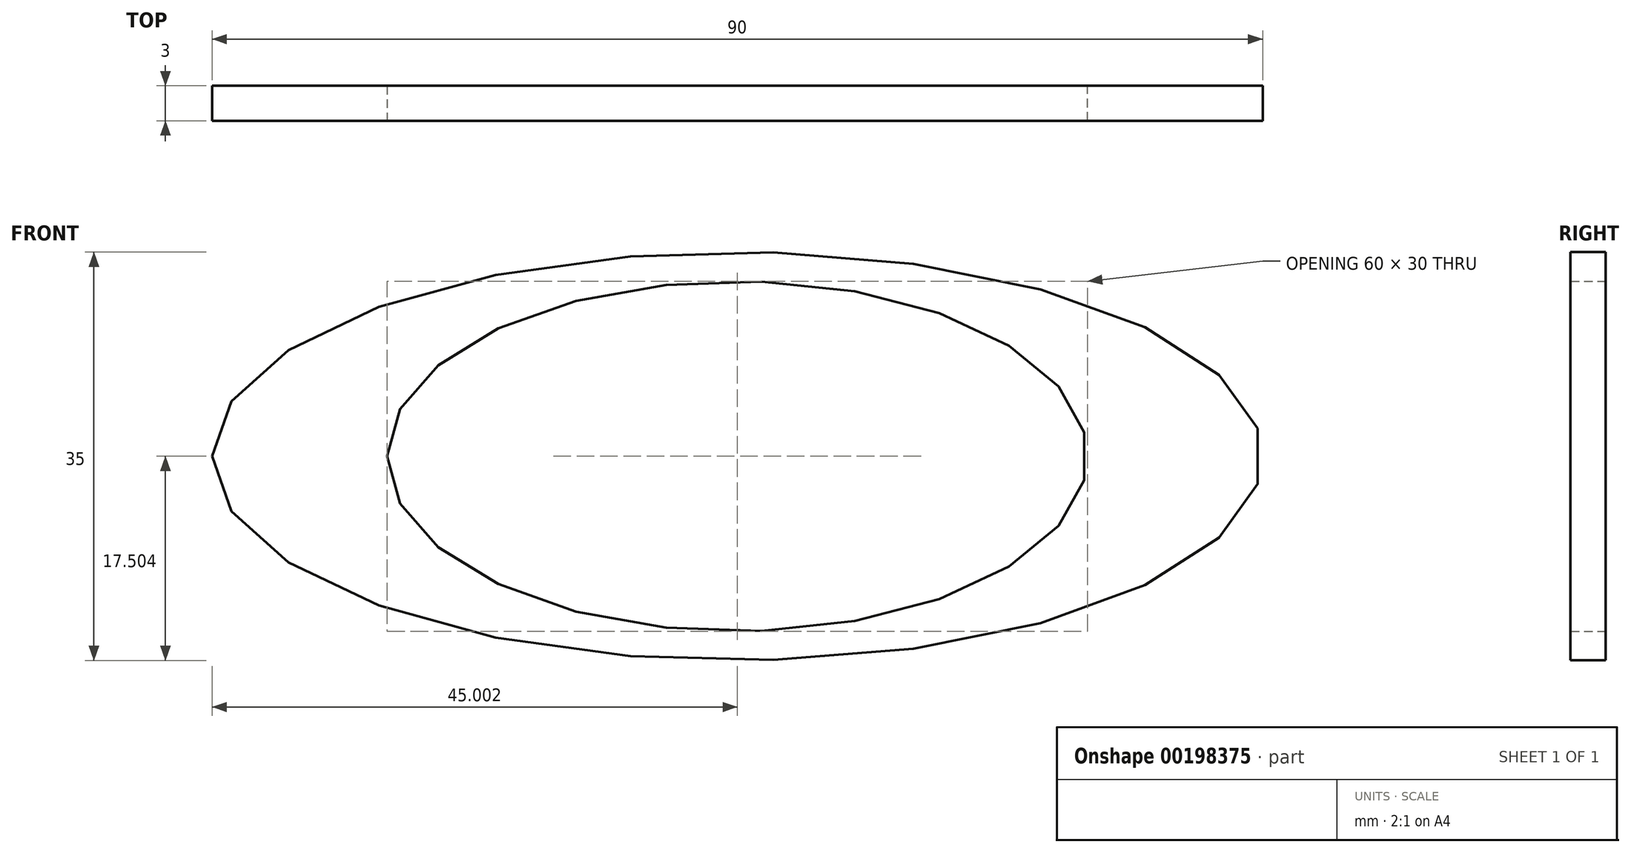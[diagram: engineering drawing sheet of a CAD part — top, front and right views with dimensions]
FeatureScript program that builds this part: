
annotation { "Feature Type Name" : "Feature", "Feature Type Description" : "" }
export const myFeature = defineFeature(function(context is Context, id is Id, definition is map)
    precondition{}
    {
        {
            var Q0;
            Q0=qCreatedBy(makeId("Front.planeOp"),FACE);
            var sketch = newSketch(context, id + "F0", { "sketchPlane" : qUnion([Q0])});
            skEllipse(sketch, "E0", {"center": v(-9.7, -46.2) * mm, "majorRadius": 45 * mm, "minorRadius": 17.5 * mm, "majorAxis": v(-1, 0)});
            skSolve(sketch);
        }
        {
            var Q0;
            Q0=qSketchRegion(id+"F0",true);
            extrude(context, id + "F1", {"entities" : qUnion([Q0]), "depth" : 3 * mm});
        }
        {
            var Q0;
            Q0=makeQuery(id+"F1.opExtrude","CAP_FACE",FACE,{"disambiguationData":[OSD([sQuery(id+"F0.wireOp",EDGE,"E0")])],"isStart":false});
            var sketch = newSketch(context, id + "F2", { "sketchPlane" : qUnion([Q0])});
            skEllipse(sketch, "E1", {"center": v(-9.7, -46.2) * mm, "majorRadius": 30 * mm, "minorRadius": 15 * mm, "majorAxis": v(-1, 0)});
            skSolve(sketch);
        }
        {
            var Q0;
            Q0 = qSketchRegion(id + "F2", true);
            extrude(context, id + "F3", {"entities" : qUnion([Q0]), "operationType" : NewBodyOperationType.REMOVE, "endBound" : BoundingType.THROUGH_ALL, "oppositeDirection" : true, "depth" : 25 * mm});
        }
    });
